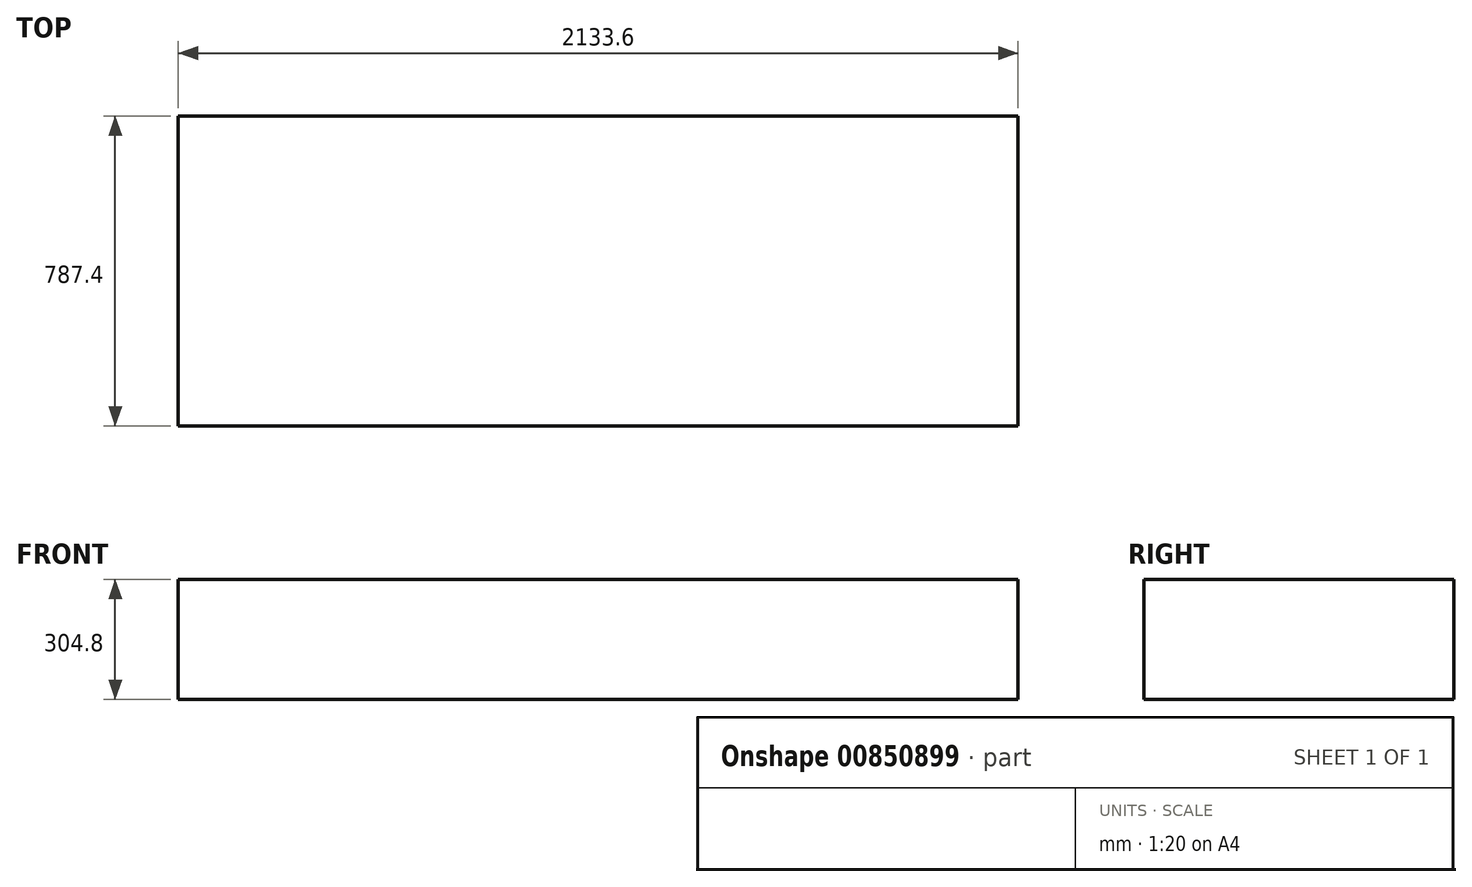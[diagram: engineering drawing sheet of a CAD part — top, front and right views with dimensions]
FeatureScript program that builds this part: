
annotation { "Feature Type Name" : "Feature", "Feature Type Description" : "" }
export const myFeature = defineFeature(function(context is Context, id is Id, definition is map)
    precondition{}
    {
        {
            var Q0;
            Q0=qCreatedBy(makeId("Top.planeOp"),FACE);
            var sketch = newSketch(context, id + "F0", { "sketchPlane" : qUnion([Q0])});
            skLineSegment(sketch, "E0.bottom", {"start": v(0, 0) * mm, "end": v(2133.6, 0) * mm});
            skLineSegment(sketch, "E0.top", {"start": v(0, -787.4) * mm, "end": v(2133.6, -787.4) * mm});
            skLineSegment(sketch, "E0.left", {"start": v(0, 0) * mm, "end": v(0, -787.4) * mm});
            skLineSegment(sketch, "E0.right", {"start": v(2133.6, 0) * mm, "end": v(2133.6, -787.4) * mm});
            skSolve(sketch);
        }
        {
            var Q0;
            Q0=makeQuery(id+"F0.imprint","IMPRINT",FACE,{"disambiguationData":[TD([[makeQuery(id+"F0.imprint","IMPRINT",EDGE,{"derivedFrom":sQuery(id+"F0.wireOp",EDGE,"E0.bottom")}),-1.0]])]});
            extrude(context, id + "F1", {"entities" : qUnion([Q0]), "depth" : 304.8 * mm, "offsetDistance" : 25.4 * mm});
        }
        {
            var Q0;
            Q0=qCreatedBy(makeId("Top.planeOp"),FACE);
            var sketch = newSketch(context, id + "F2", { "sketchPlane" : qUnion([Q0])});
            skLineSegment(sketch, "E1.bottom", {"start": v(0, 0) * mm, "end": v(152.4, 0) * mm});
            skLineSegment(sketch, "E1.top", {"start": v(0, -152.4) * mm, "end": v(152.4, -152.4) * mm});
            skLineSegment(sketch, "E1.left", {"start": v(0, 0) * mm, "end": v(0, -152.4) * mm});
            skLineSegment(sketch, "E1.right", {"start": v(152.4, 0) * mm, "end": v(152.4, -152.4) * mm});
            skSolve(sketch);
        }
        {
            var Q0;
            Q0=makeQuery(id+"F2.imprint","IMPRINT",FACE,{"disambiguationData":[TD([[makeQuery(id+"F2.imprint","IMPRINT",EDGE,{"derivedFrom":sQuery(id+"F2.wireOp",EDGE,"E1.bottom")}),-1.0]])]});
            extrude(context, id + "F3", {"entities" : qUnion([Q0]), "depth" : 6.35 * mm, "offsetDistance" : 25.4 * mm});
        }
        {
            var Q0;
            Q0=makeQuery(id+"F3.opExtrude","CAP_FACE",FACE,{"disambiguationData":[OSD([sQuery(id+"F2.wireOp",EDGE,"E1.bottom"),sQuery(id+"F2.wireOp",EDGE,"E1.top"),sQuery(id+"F2.wireOp",EDGE,"E1.left"),sQuery(id+"F2.wireOp",EDGE,"E1.right")])],"isStart":false});
            var sketch = newSketch(context, id + "F4", { "sketchPlane" : qUnion([Q0])});
            skLineSegment(sketch, "E2", {"start": v(50.13, -88.16) * mm, "end": v(56.48, -88.16) * mm});
            skLineSegment(sketch, "E3", {"start": v(56.48, -88.16) * mm, "end": v(56.48, -53.24) * mm});
            skLineSegment(sketch, "E4", {"start": v(56.48, -53.24) * mm, "end": v(97.75, -53.24) * mm});
            skLineSegment(sketch, "E5", {"start": v(97.75, -53.24) * mm, "end": v(97.75, -88.16) * mm});
            skLineSegment(sketch, "E6", {"start": v(97.75, -88.16) * mm, "end": v(104.1, -88.16) * mm});
            skLineSegment(sketch, "E7", {"start": v(104.1, -88.16) * mm, "end": v(104.1, -46.89) * mm});
            skLineSegment(sketch, "E8", {"start": v(104.1, -46.89) * mm, "end": v(50.13, -46.89) * mm});
            skLineSegment(sketch, "E9", {"start": v(50.13, -46.89) * mm, "end": v(50.13, -88.16) * mm});
            skLineSegment(sketch, "E10", {"start": v(76.2, 0) * mm, "end": v(76.2, -152.4) * mm, "construction": true});
            skSolve(sketch);
        }
        {
            var Q0;
            Q0 = qSketchRegion(id + "F4", true);
            extrude(context, id + "F5", {"entities" : qUnion([Q0]), "operationType" : NewBodyOperationType.ADD, "depth" : 41.27 * mm, "offsetDistance" : 25.4 * mm});
        }
    });
